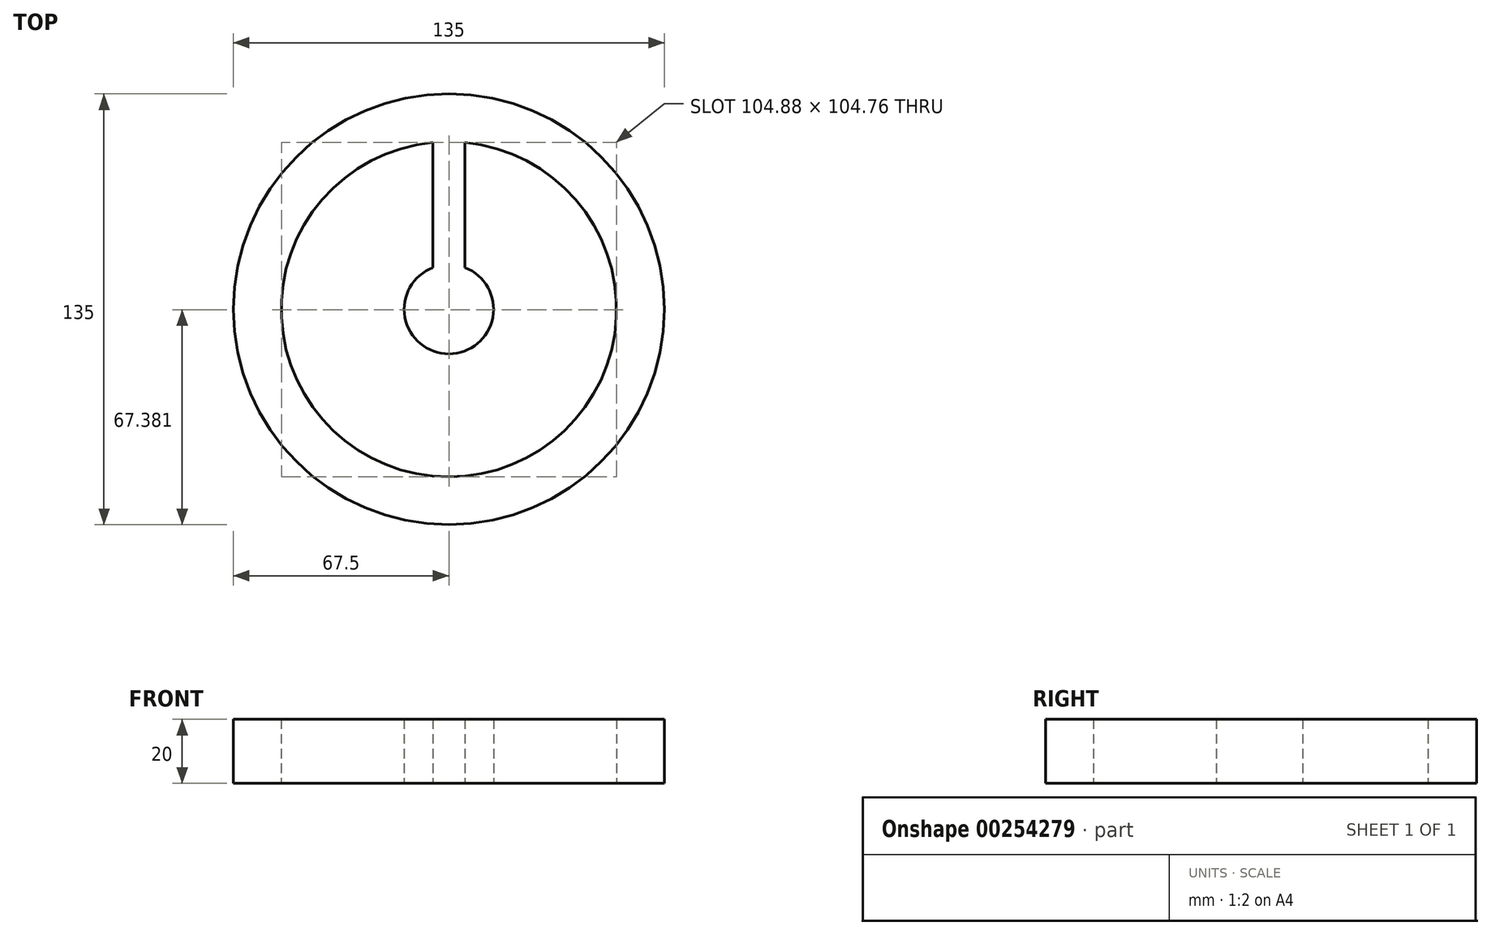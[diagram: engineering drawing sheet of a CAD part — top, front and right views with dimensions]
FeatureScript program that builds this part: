
annotation { "Feature Type Name" : "Feature", "Feature Type Description" : "" }
export const myFeature = defineFeature(function(context is Context, id is Id, definition is map)
    precondition{}
    {
        {
            assignVariable(context, id + "F0", {"variableType" : VariableType.LENGTH, "name" : "w", "lengthValue" : 20 * mm});
        }
        {
            var Q0;
            Q0=qCreatedBy(makeId("Top.planeOp"),FACE);
            var sketch = newSketch(context, id + "F1", { "sketchPlane" : qUnion([Q0])});
            skCircle(sketch, "E0", {"center": v(0, 0) * mm, "radius": 67.5 * mm});
            skCircle(sketch, "E1", {"center": v(0, 0) * mm, "radius": 52.5 * mm});
            skSolve(sketch);
        }
        {
            var Q0;
            Q0=makeQuery(id+"F1.imprint","IMPRINT",FACE,{"disambiguationData":[TD([[makeQuery(id+"F1.imprint","IMPRINT",EDGE,{"derivedFrom":sQuery(id+"F1.wireOp",EDGE,"E0")}),1.0]])]});
            extrude(context, id + "F2", {"entities" : qUnion([Q0]), "depth" : getVariable(context, 'w'), "offsetDistance" : 25 * mm});
        }
        {
            var Q0;
            Q0=qCreatedBy(makeId("Top.planeOp"),FACE);
            var sketch = newSketch(context, id + "F3", { "sketchPlane" : qUnion([Q0])});
            skCircle(sketch, "E2", {"center": v(0, 0) * mm, "radius": 14 * mm});
            skSolve(sketch);
        }
        {
            var Q0;
            Q0=makeQuery(id+"F3.imprint","IMPRINT",FACE,{"disambiguationData":[TD([[makeQuery(id+"F3.imprint","IMPRINT",EDGE,{"derivedFrom":sQuery(id+"F3.wireOp",EDGE,"E2")}),1.0]])]});
            extrude(context, id + "F4", {"entities" : qUnion([Q0]), "depth" : getVariable(context, 'w'), "offsetDistance" : 25 * mm});
        }
        {
            var Q0;
            Q0=qCreatedBy(makeId("Top.planeOp"),FACE);
            var sketch = newSketch(context, id + "F5", { "sketchPlane" : qUnion([Q0])});
            skLineSegment(sketch, "E3", {"start": v(0, 0) * mm, "end": v(0, 67.5) * mm, "construction": true});
            skLineSegment(sketch, "E4", {"start": v(-5, 52.5) * mm, "end": v(-5, 13.08) * mm});
            skLineSegment(sketch, "E5", {"start": v(-5, 13.08) * mm, "end": v(5, 13.08) * mm});
            skLineSegment(sketch, "E6", {"start": v(5, 13.08) * mm, "end": v(5, 52.5) * mm});
            skPoint(sketch, "E7", {"position": v(0, 13.08) * mm});
            skLineSegment(sketch, "E8", {"start": v(-5, 52.5) * mm, "end": v(5, 52.5) * mm});
            skSolve(sketch);
        }
        {
            var Q0;
            Q0=makeQuery(id+"F5.imprint","IMPRINT",FACE,{"disambiguationData":[TD([[makeQuery(id+"F5.imprint","IMPRINT",EDGE,{"derivedFrom":sQuery(id+"F5.wireOp",EDGE,"E4")}),1.0]])]});
            extrude(context, id + "F6", {"entities" : qUnion([Q0]), "operationType" : NewBodyOperationType.ADD, "depth" : getVariable(context, 'w'), "offsetDistance" : 25 * mm});
        }
    });
